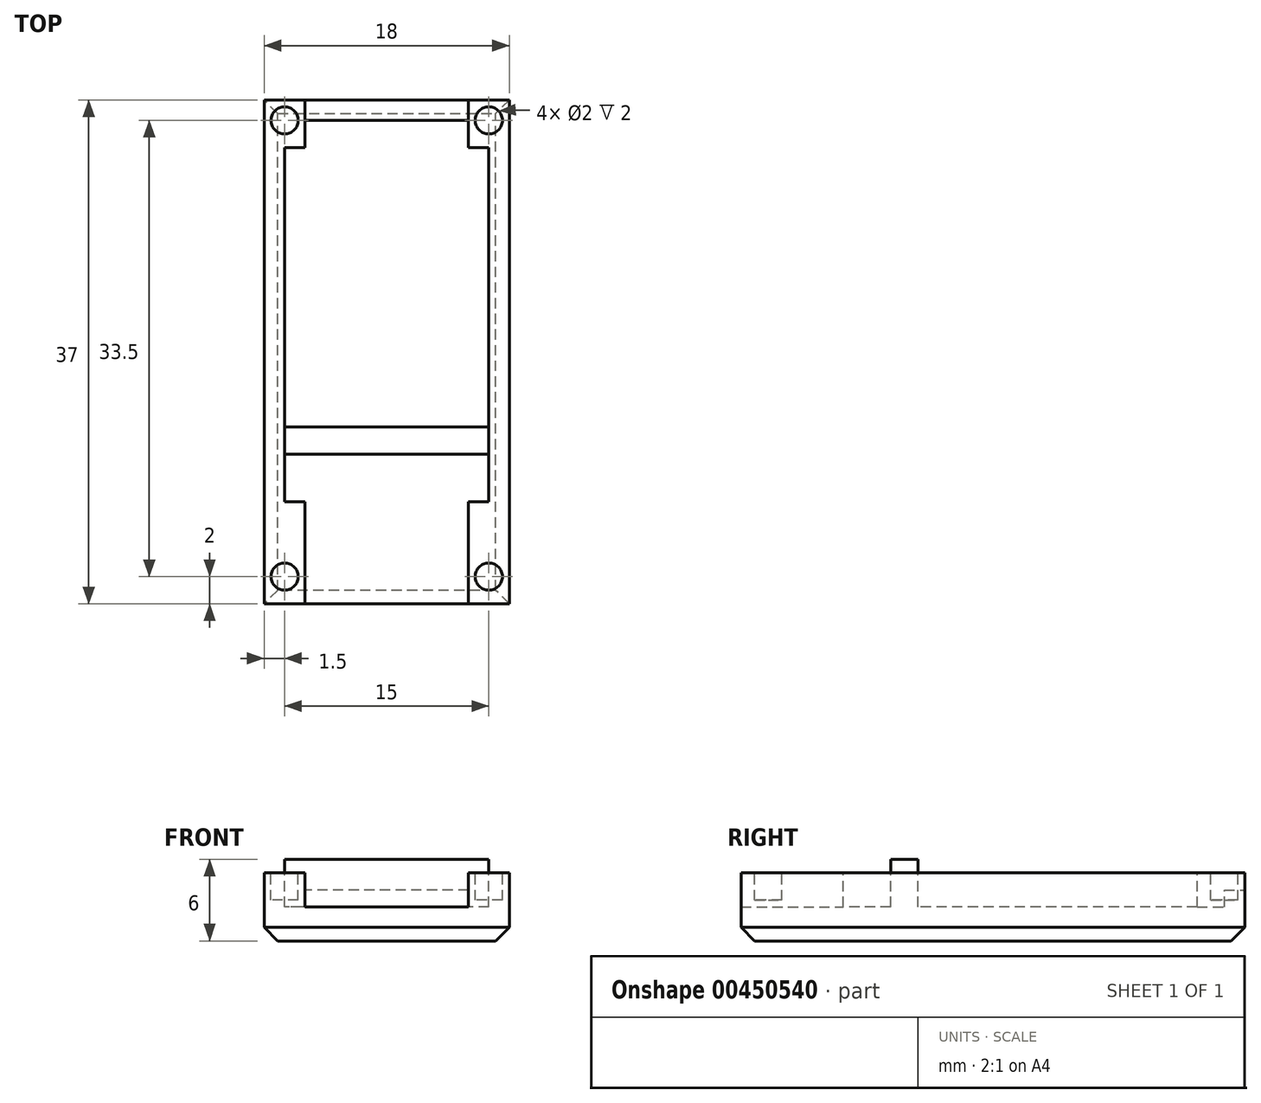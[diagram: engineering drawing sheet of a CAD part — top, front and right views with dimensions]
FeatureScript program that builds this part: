
annotation { "Feature Type Name" : "Feature", "Feature Type Description" : "" }
export const myFeature = defineFeature(function(context is Context, id is Id, definition is map)
    precondition{}
    {
        {
            var Q0;
            Q0=qCreatedBy(makeId("Front.planeOp"),FACE);
            var sketch = newSketch(context, id + "F0", { "sketchPlane" : qUnion([Q0])});
            skLineSegment(sketch, "E0.bottom", {"start": v(-8, 0) * mm, "end": v(8, 0) * mm});
            skLineSegment(sketch, "E0.top", {"start": v(-6, 2.5) * mm, "end": v(6, 2.5) * mm});
            skLineSegment(sketch, "E1.top", {"start": v(6, 5) * mm, "end": v(9, 5) * mm});
            skLineSegment(sketch, "E1.left", {"start": v(6, 2.5) * mm, "end": v(6, 5) * mm});
            skLineSegment(sketch, "E1.right", {"start": v(9, 1) * mm, "end": v(9, 5) * mm});
            skLineSegment(sketch, "E2.top", {"start": v(-6, 5) * mm, "end": v(-9, 5) * mm});
            skLineSegment(sketch, "E2.left", {"start": v(-6, 2.5) * mm, "end": v(-6, 5) * mm});
            skLineSegment(sketch, "E2.right", {"start": v(-9, 1) * mm, "end": v(-9, 5) * mm});
            skLineSegment(sketch, "E3", {"start": v(-9, 1) * mm, "end": v(-8, 0) * mm});
            skLineSegment(sketch, "E4", {"start": v(8, 0) * mm, "end": v(9, 1) * mm});
            skSolve(sketch);
        }
        {
            var Q0;
            Q0=makeQuery(id+"F0.imprint","IMPRINT",FACE,{"disambiguationData":[TD([[makeQuery(id+"F0.imprint","IMPRINT",EDGE,{"derivedFrom":sQuery(id+"F0.wireOp",EDGE,"E0.bottom")}),1.0]])]});
            extrude(context, id + "F1", {"entities" : qUnion([Q0]), "depth" : 37 * mm});
        }
        {
            var Q0;
            Q0=makeQuery(id+"F1.opExtrude","CAP_FACE",FACE,{"disambiguationData":[OSD([sQuery(id+"F0.wireOp",EDGE,"E0.bottom"),sQuery(id+"F0.wireOp",EDGE,"E0.top"),sQuery(id+"F0.wireOp",EDGE,"E1.top"),sQuery(id+"F0.wireOp",EDGE,"E1.left"),sQuery(id+"F0.wireOp",EDGE,"E1.right"),sQuery(id+"F0.wireOp",EDGE,"E2.top"),sQuery(id+"F0.wireOp",EDGE,"E2.left"),sQuery(id+"F0.wireOp",EDGE,"E2.right"),sQuery(id+"F0.wireOp",EDGE,"E3"),sQuery(id+"F0.wireOp",EDGE,"E4")])],"isStart":true});
            var sketch = newSketch(context, id + "F2", { "sketchPlane" : qUnion([Q0])});
            skLineSegment(sketch, "E5.bottom", {"start": v(-6, 2.5) * mm, "end": v(6, 2.5) * mm});
            skLineSegment(sketch, "E5.top", {"start": v(-6, 3.75) * mm, "end": v(6, 3.75) * mm});
            skLineSegment(sketch, "E5.left", {"start": v(-6, 2.5) * mm, "end": v(-6, 3.75) * mm});
            skLineSegment(sketch, "E5.right", {"start": v(6, 2.5) * mm, "end": v(6, 3.75) * mm});
            skSolve(sketch);
        }
        {
            var Q0;
            Q0=makeQuery(id+"F2.imprint","IMPRINT",FACE,{"disambiguationData":[TD([[makeQuery(id+"F2.imprint","IMPRINT",EDGE,{"derivedFrom":sQuery(id+"F2.wireOp",EDGE,"E5.bottom")}),-1.0]])]});
            extrude(context, id + "F3", {"entities" : qUnion([Q0]), "operationType" : NewBodyOperationType.ADD, "oppositeDirection" : true, "depth" : 2 * mm});
        }
        {
            var Q0;
            Q0=makeQuery(id+"F1.opExtrude","SWEPT_FACE",FACE,{"disambiguationData":[OSD([sQuery(id+"F0.wireOp",EDGE,"E2.top")])]});
            var sketch = newSketch(context, id + "F4", { "sketchPlane" : qUnion([Q0])});
            skLineSegment(sketch, "E6.top", {"start": v(-7.5, -29.5) * mm, "end": v(-6, -29.5) * mm});
            skLineSegment(sketch, "E6.right", {"start": v(-6, -35.5) * mm, "end": v(-6, -29.5) * mm});
            skLineSegment(sketch, "E7.bottom", {"start": v(7.5, -35.5) * mm, "end": v(6, -35.5) * mm, "construction": true});
            skLineSegment(sketch, "E7.top", {"start": v(7.5, -29.5) * mm, "end": v(6, -29.5) * mm});
            skLineSegment(sketch, "E7.right", {"start": v(6, -35.5) * mm, "end": v(6, -29.5) * mm});
            skLineSegment(sketch, "E8", {"start": v(-6, -35.5) * mm, "end": v(6, -35.5) * mm});
            skLineSegment(sketch, "E9", {"start": v(-6, -35.5) * mm, "end": v(-7.5, -35.5) * mm, "construction": true});
            skLineSegment(sketch, "E10", {"start": v(7.5, -35.5) * mm, "end": v(7.5, -29.5) * mm, "construction": true});
            skLineSegment(sketch, "E11.top", {"start": v(-7.5, -3.5) * mm, "end": v(-6, -3.5) * mm});
            skLineSegment(sketch, "E11.left", {"start": v(-7.5, -1.5) * mm, "end": v(-7.5, -3.5) * mm, "construction": true});
            skLineSegment(sketch, "E11.right", {"start": v(-6, -1.5) * mm, "end": v(-6, -3.5) * mm});
            skLineSegment(sketch, "E12.bottom", {"start": v(7.5, -1.5) * mm, "end": v(6, -1.5) * mm, "construction": true});
            skLineSegment(sketch, "E12.top", {"start": v(7.5, -3.5) * mm, "end": v(6, -3.5) * mm});
            skLineSegment(sketch, "E12.right", {"start": v(6, -1.5) * mm, "end": v(6, -3.5) * mm});
            skLineSegment(sketch, "E13", {"start": v(-6, -3.5) * mm, "end": v(6, -3.5) * mm, "construction": true});
            skLineSegment(sketch, "E14", {"start": v(-6, -1.5) * mm, "end": v(6, -1.5) * mm});
            skLineSegment(sketch, "E15", {"start": v(-7.5, -1.5) * mm, "end": v(-6, -1.5) * mm, "construction": true});
            skLineSegment(sketch, "E16", {"start": v(-7.5, -35.5) * mm, "end": v(-7.5, -29.5) * mm, "construction": true});
            skLineSegment(sketch, "E17", {"start": v(-7.5, -29.5) * mm, "end": v(-7.5, -3.5) * mm});
            skLineSegment(sketch, "E18", {"start": v(7.5, -29.5) * mm, "end": v(7.5, -3.5) * mm});
            skLineSegment(sketch, "E19", {"start": v(7.5, -3.5) * mm, "end": v(7.5, -1.5) * mm, "construction": true});
            skSolve(sketch);
        }
        {
            var Q0;
            Q0 = qSketchRegion(id + "F4", true);
            var Q1;
            Q1=makeQuery(id+"F1.opExtrude","SWEPT_FACE",FACE,{"disambiguationData":[OSD([sQuery(id+"F0.wireOp",EDGE,"E0.top")])]});
            extrude(context, id + "F5", {"entities" : qUnion([Q0]), "operationType" : NewBodyOperationType.REMOVE, "endBound" : BoundingType.UP_TO_SURFACE, "oppositeDirection" : true, "endBoundEntityFace" : qUnion([Q1]), "depth" : 25.4 * mm});
        }
        {
            var Q0;
            {var subQ0=sQuery(id+"F0.wireOp",EDGE,"E0.top");Q0=makeQuery(id+"F5.boolean.opBoolean","MERGE",FACE,{"derivedFrom":[makeQuery(id+"F1.opExtrude","SWEPT_FACE",FACE,{"disambiguationData":[OSD([subQ0])]}),makeQuery(id+"F5.opExtrude","CAP_FACE",FACE,{"disambiguationData":[OSD([subQ0])],"isStart":false})]});}
            cPlane(context, id + "F6", {"entities" : qUnion([Q0]), "cplaneType" : CPlaneType.OFFSET, "offset" : 3.5 * mm, "width" : 152.4 * mm, "height" : 152.4 * mm});
        }
        {
            var Q0;
            Q0=qCreatedBy(id+"F6.planeOp",FACE);
            var sketch = newSketch(context, id + "F7", { "sketchPlane" : qUnion([Q0])});
            skLineSegment(sketch, "E20.bottom", {"start": v(-7.5, -24) * mm, "end": v(7.5, -24) * mm});
            skLineSegment(sketch, "E20.top", {"start": v(-7.5, -26) * mm, "end": v(7.5, -26) * mm});
            skLineSegment(sketch, "E20.left", {"start": v(-7.5, -24) * mm, "end": v(-7.5, -26) * mm});
            skLineSegment(sketch, "E20.right", {"start": v(7.5, -24) * mm, "end": v(7.5, -26) * mm});
            skSolve(sketch);
        }
        {
            var Q0;
            Q0=makeQuery(id+"F7.imprint","IMPRINT",FACE,{"disambiguationData":[TD([[makeQuery(id+"F7.imprint","IMPRINT",EDGE,{"derivedFrom":sQuery(id+"F7.wireOp",EDGE,"E20.bottom")}),-1.0]])]});
            var Q1;
            {var subQ0=sQuery(id+"F0.wireOp",EDGE,"E0.top");Q1=makeQuery(id+"F5.boolean.opBoolean","MERGE",FACE,{"derivedFrom":[makeQuery(id+"F1.opExtrude","SWEPT_FACE",FACE,{"disambiguationData":[OSD([subQ0])]}),makeQuery(id+"F5.opExtrude","CAP_FACE",FACE,{"disambiguationData":[OSD([subQ0])],"isStart":false})]});}
            extrude(context, id + "F8", {"entities" : qUnion([Q0]), "operationType" : NewBodyOperationType.ADD, "endBound" : BoundingType.UP_TO_SURFACE, "oppositeDirection" : true, "endBoundEntityFace" : qUnion([Q1]), "depth" : 25.4 * mm});
        }
        {
            var Q0;
            Q0=makeQuery(id+"F1.opExtrude","SWEPT_FACE",FACE,{"disambiguationData":[OSD([sQuery(id+"F0.wireOp",EDGE,"E2.top")])]});
            var sketch = newSketch(context, id + "F9", { "sketchPlane" : qUnion([Q0])});
            skCircle(sketch, "E21", {"center": v(-7.5, -35) * mm, "radius": 1 * mm});
            skCircle(sketch, "E22", {"center": v(134.64, -34.77) * mm, "radius": 0.93 * mm});
            skCircle(sketch, "E23", {"center": v(7.5, -35) * mm, "radius": 1 * mm});
            skCircle(sketch, "E24", {"center": v(-7.5, -1.5) * mm, "radius": 1 * mm});
            skCircle(sketch, "E25", {"center": v(7.5, -1.5) * mm, "radius": 1 * mm});
            skSolve(sketch);
        }
        {
            var Q0;
            Q0 = qSketchRegion(id + "F9", true);
            extrude(context, id + "F10", {"entities" : qUnion([Q0]), "operationType" : NewBodyOperationType.REMOVE, "oppositeDirection" : true, "depth" : 2 * mm});
        }
        {
            var Q0;
            Q0=makeQuery(id+"F1.opExtrude","CAP_EDGE",EDGE,{"disambiguationData":[OSD([sQuery(id+"F0.wireOp",EDGE,"E0.bottom")])],"isStart":true});
            var Q1;
            Q1=makeQuery(id+"F1.opExtrude","CAP_EDGE",EDGE,{"disambiguationData":[OSD([sQuery(id+"F0.wireOp",EDGE,"E0.bottom")])],"isStart":false});
            chamfer(context, id + "F11", {"entities" : qUnion([Q0, Q1]), "width" : 1 * mm, "tangentPropagation" : true});
        }
    });
